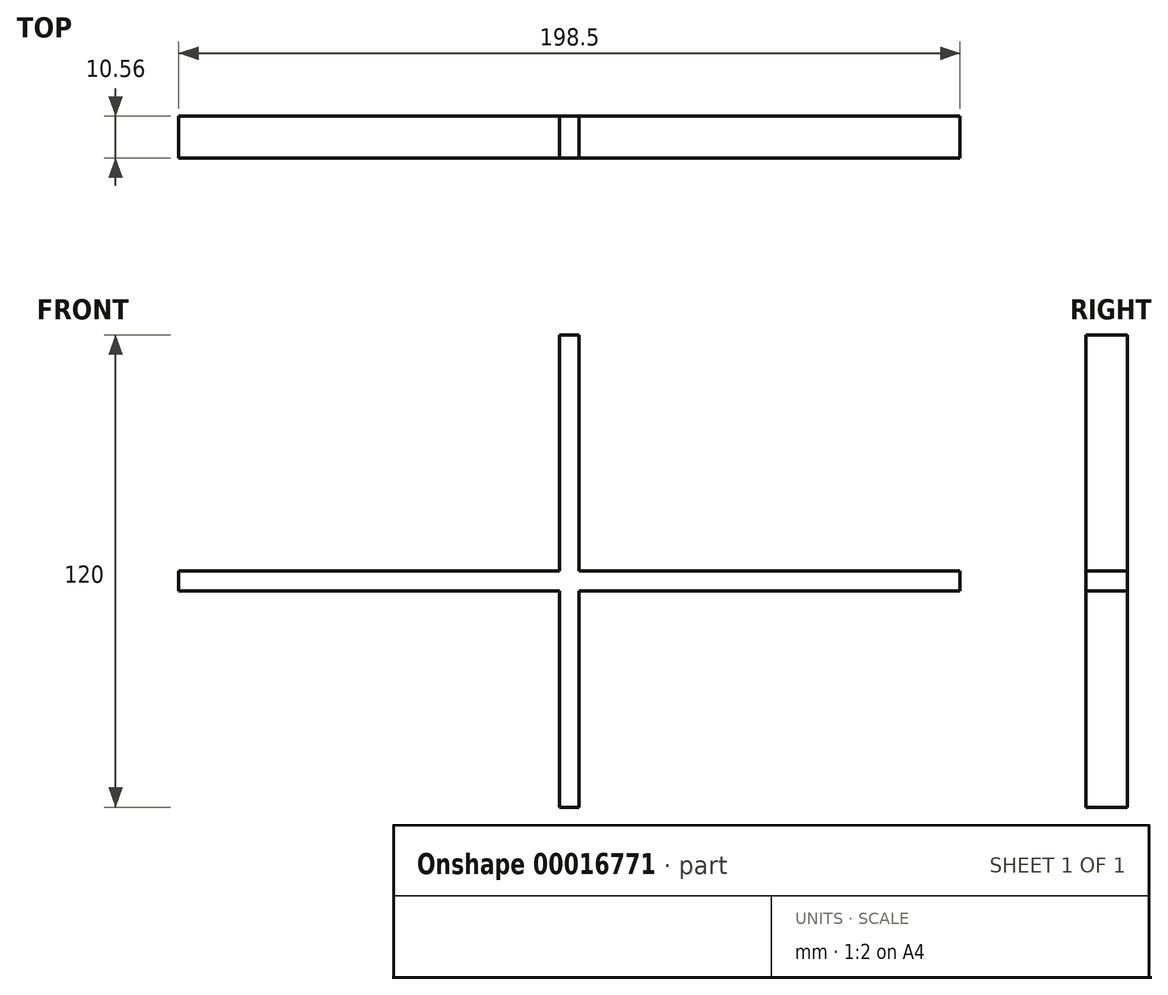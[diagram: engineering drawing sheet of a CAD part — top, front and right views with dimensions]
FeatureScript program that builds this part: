
annotation { "Feature Type Name" : "Feature", "Feature Type Description" : "" }
export const myFeature = defineFeature(function(context is Context, id is Id, definition is map)
    precondition{}
    {
        {
            var Q0;
            Q0=qCreatedBy(makeId("Top.planeOp"),FACE);
            var sketch = newSketch(context, id + "F0", { "sketchPlane" : qUnion([Q0])});
            skLineSegment(sketch, "E0.rect.bottom", {"start": v(99.25, -5.28) * mm, "end": v(-99.25, -5.28) * mm});
            skLineSegment(sketch, "E0.rect.top", {"start": v(99.25, 5.28) * mm, "end": v(-99.25, 5.28) * mm});
            skLineSegment(sketch, "E0.rect.left", {"start": v(99.25, -5.28) * mm, "end": v(99.25, 5.28) * mm});
            skLineSegment(sketch, "E0.rect.right", {"start": v(-99.25, -5.28) * mm, "end": v(-99.25, 5.28) * mm});
            skPoint(sketch, "E0.rect.middle", {"position": v(0, 0) * mm});
            skSolve(sketch);
        }
        {
            var Q0;
            Q0=makeQuery(id+"F0.imprint","IMPRINT",FACE,{"disambiguationData":[TD([[makeQuery(id+"F0.imprint","IMPRINT",EDGE,{"derivedFrom":sQuery(id+"F0.wireOp",EDGE,"E0.rect.bottom")}),-1.0]])]});
            extrude(context, id + "F1", {"entities" : qUnion([Q0]), "depth" : 5 * mm});
        }
        {
            var Q0;
            Q0=makeQuery(id+"F1.opExtrude","CAP_FACE",FACE,{"disambiguationData":[OSD([sQuery(id+"F0.wireOp",EDGE,"E0.rect.bottom"),sQuery(id+"F0.wireOp",EDGE,"E0.rect.top"),sQuery(id+"F0.wireOp",EDGE,"E0.rect.left"),sQuery(id+"F0.wireOp",EDGE,"E0.rect.right")])],"isStart":false});
            var sketch = newSketch(context, id + "F2", { "sketchPlane" : qUnion([Q0])});
            skLineSegment(sketch, "E1.rect.bottom", {"start": v(2.5, 5.28) * mm, "end": v(-2.5, 5.28) * mm});
            skLineSegment(sketch, "E1.rect.top", {"start": v(2.5, -5.28) * mm, "end": v(-2.5, -5.28) * mm});
            skLineSegment(sketch, "E1.rect.left", {"start": v(2.5, 5.28) * mm, "end": v(2.5, -5.28) * mm});
            skLineSegment(sketch, "E1.rect.right", {"start": v(-2.5, 5.28) * mm, "end": v(-2.5, -5.28) * mm});
            skPoint(sketch, "E1.rect.middle", {"position": v(0, 0) * mm});
            skSolve(sketch);
        }
        {
            var Q0;
            Q0=makeQuery(id+"F2.imprint","IMPRINT",FACE,{"disambiguationData":[TD([[makeQuery(id+"F2.imprint","IMPRINT",EDGE,{"derivedFrom":sQuery(id+"F2.wireOp",EDGE,"E1.rect.bottom")}),1.0]])]});
            extrude(context, id + "F3", {"entities" : qUnion([Q0]), "operationType" : NewBodyOperationType.ADD, "depth" : 120 * mm, "symmetric" : true});
        }
    });
